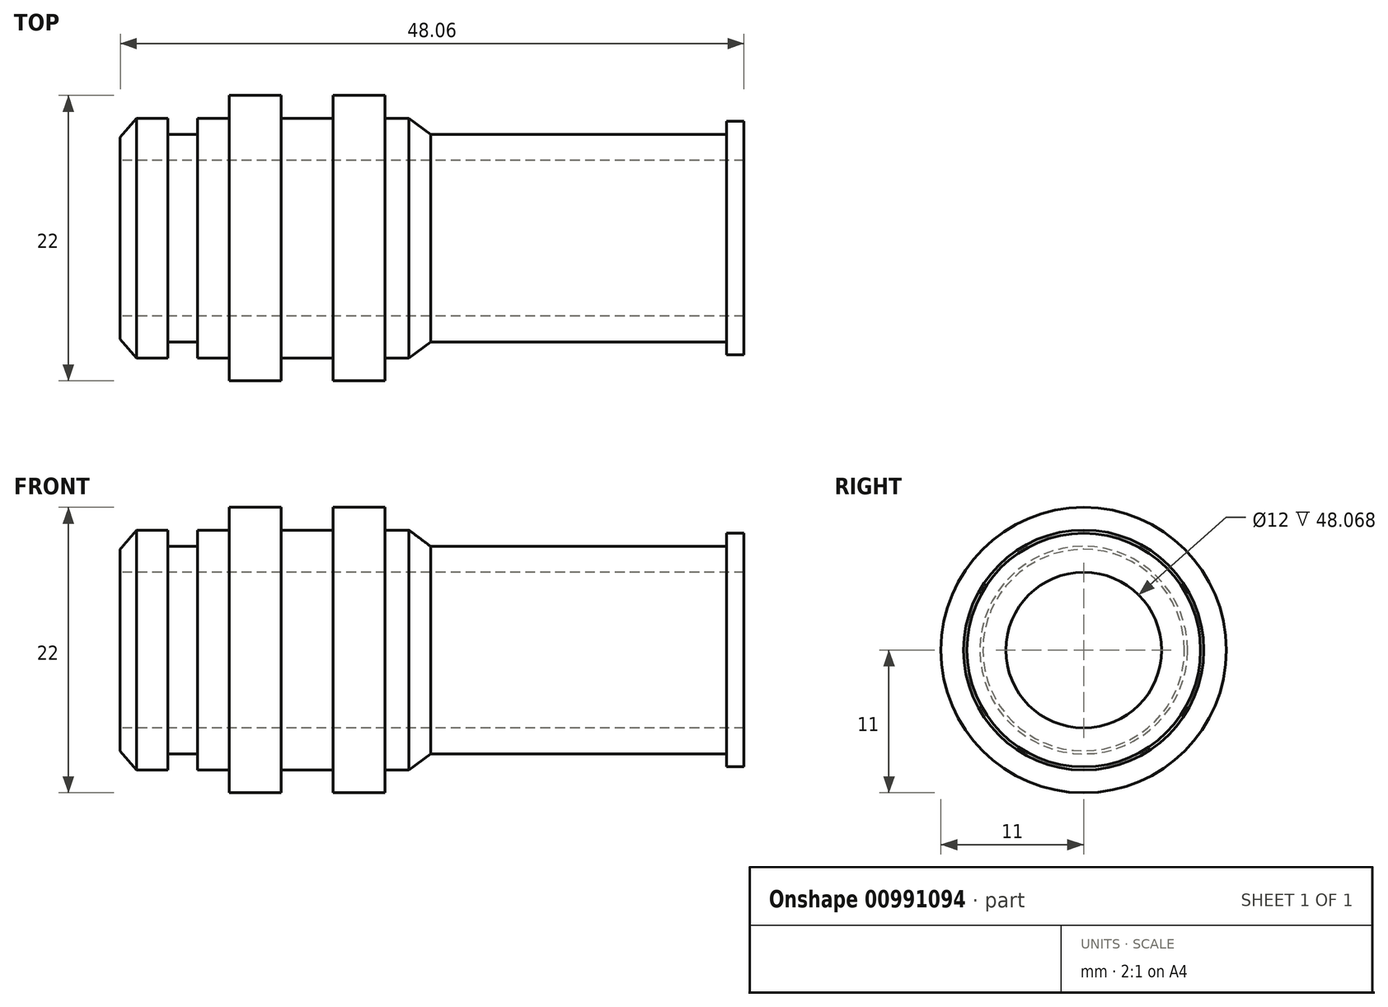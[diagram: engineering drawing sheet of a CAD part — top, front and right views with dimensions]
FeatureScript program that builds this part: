
annotation { "Feature Type Name" : "Feature", "Feature Type Description" : "" }
export const myFeature = defineFeature(function(context is Context, id is Id, definition is map)
    precondition{}
    {
        {
            var Q0;
            Q0=qCreatedBy(makeId("Top.planeOp"),FACE);
            var sketch = newSketch(context, id + "F0", { "sketchPlane" : qUnion([Q0])});
            skLineSegment(sketch, "E0", {"start": v(0, 0) * mm, "end": v(53.24, 0) * mm, "construction": true});
            skSolve(sketch);
        }
        {
            var Q0;
            Q0=qCreatedBy(makeId("Top.planeOp"),FACE);
            var sketch = newSketch(context, id + "F1", { "sketchPlane" : qUnion([Q0])});
            skLineSegment(sketch, "E1", {"start": v(-6.16, 11) * mm, "end": v(-2.16, 11) * mm});
            skLineSegment(sketch, "E2", {"start": v(33.5, 6) * mm, "end": v(-14.56, 6) * mm});
            skLineSegment(sketch, "E3", {"start": v(-53.65, 9.25) * mm, "end": v(81.35, 9.25) * mm, "construction": true});
            skLineSegment(sketch, "E4", {"start": v(-14.56, 6) * mm, "end": v(-14.56, 7.77) * mm});
            skLineSegment(sketch, "E5", {"start": v(-14.56, 7.77) * mm, "end": v(-13.3, 9.25) * mm});
            skLineSegment(sketch, "E6", {"start": v(-13.3, 9.25) * mm, "end": v(-10.88, 9.25) * mm});
            skLineSegment(sketch, "E7", {"start": v(-10.88, 9.25) * mm, "end": v(-10.88, 8) * mm});
            skLineSegment(sketch, "E8", {"start": v(-10.88, 8) * mm, "end": v(-8.6, 8) * mm});
            skLineSegment(sketch, "E9", {"start": v(-8.6, 8) * mm, "end": v(-8.6, 9.25) * mm});
            skLineSegment(sketch, "E10", {"start": v(-8.6, 9.25) * mm, "end": v(-6.16, 9.25) * mm});
            skLineSegment(sketch, "E11", {"start": v(-6.16, 9.25) * mm, "end": v(-6.16, 11) * mm});
            skLineSegment(sketch, "E12", {"start": v(-2.16, 11) * mm, "end": v(-2.16, 9.25) * mm});
            skLineSegment(sketch, "E13", {"start": v(7.69, 9.25) * mm, "end": v(9.35, 8) * mm});
            skLineSegment(sketch, "E14", {"start": v(9.35, 8) * mm, "end": v(32.15, 8) * mm});
            skLineSegment(sketch, "E15", {"start": v(-2.16, 9.25) * mm, "end": v(1.84, 9.25) * mm});
            skLineSegment(sketch, "E16", {"start": v(1.84, 9.25) * mm, "end": v(1.84, 11) * mm});
            skLineSegment(sketch, "E17", {"start": v(1.84, 11) * mm, "end": v(5.84, 11) * mm});
            skLineSegment(sketch, "E18", {"start": v(5.84, 11) * mm, "end": v(5.84, 9.25) * mm});
            skLineSegment(sketch, "E19", {"start": v(5.84, 9.25) * mm, "end": v(7.69, 9.25) * mm});
            skLineSegment(sketch, "E20", {"start": v(32.15, 8) * mm, "end": v(32.15, 9) * mm});
            skLineSegment(sketch, "E21", {"start": v(32.15, 9) * mm, "end": v(33.5, 9) * mm});
            skLineSegment(sketch, "E22", {"start": v(33.5, 9) * mm, "end": v(33.5, 6) * mm});
            skLineSegment(sketch, "E23", {"start": v(-23.3, 11) * mm, "end": v(38.9, 11) * mm, "construction": true});
            skSolve(sketch);
        }
        {
            var Q0;
            Q0 = qSketchRegion(id + "F1", true);
            var Q1;
            Q1=sQuery(id+"F0.wireOp",EDGE,"E0");
            revolve(context, id + "F2", {"surfaceOperationType" : NewSurfaceOperationType.NEW, "entities" : qUnion([Q0]), "axis" : qUnion([Q1]), "revolveType" : RevolveType.FULL});
        }
    });
